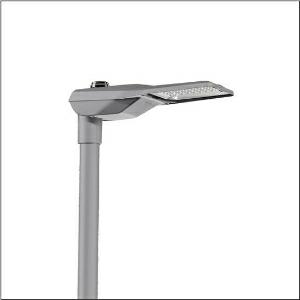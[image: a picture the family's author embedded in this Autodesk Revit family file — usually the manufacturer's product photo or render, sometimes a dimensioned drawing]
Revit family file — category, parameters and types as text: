
# Revit family: streetlight_sl_21_mini___st1_0a_5xe6d37n08hb_abde
name_source: partatom
category: Lighting Fixtures
units: mm (PartAtom-declared; Revit-internal decimal feet)

## family parameters
Cut with Voids When Loaded = No
Host = Face
Light Source = No
Part Type = Normal
Room Calculation Point = No
Round Connector Dimension = Use Diameter
Shared = No

## types (1)
- --- (1 x LED, 9040 lm, 66 W, 3000K)
    Apparent Load = 66 VA
    CIE Flux Codes = 37 72 97 100 100
    Color Rendering = 70
    Color Temperature = 3000K
    Default Elevation = 1800 mm
    Description = Streetlight SL 21 mini, mast luminaire, primary light control with lens, of PMMA, primary optical cover: cover, of toughened safety glass, transparent, light distribution: ST1.0a, light emission: direct distribution, primary light characteristic: asymmetric, installation type: side-entry, LED, 3G 1.5mm², High Power LED, rated luminous flux: 9.040lm, luminous efficacy: 137lm/W, light colour: 730, colour temperature: 3000K, control gear: NEMA (7pin), control: overheat protection, pre-setting: linear dimming characteristic, constant luminous flux control, time-dependent luminous flux control, flexible luminous flux parameterisation, mains connection: 230..240V, AC, 50/60Hz, connection cable pre-assembled, cable length: 8,5m, wiring characteristics: H07RN-F, start of lifetime: 66W, end of service life: 69W, reduction: 30W, luminaire housing, of diecast aluminium (EN AC-44300), powder-coated, Siteco® metallic grey (DB 702S), corrosivity category C5 mid according to DIN EN ISO 12944, multi-level sealing system, sealing non-destructively replaceable, inclination adjustable: 0°, 5°, 10°, 15°, length: 628mm, width: 235mm, height: 110mm, spigot size: 42mm (side-entry), mounting height: 4..8m, protection rating (complete): IP66, insulation class (complete): insulation class I (protective earthing), certification: CE, ENEC, ENEC+, VDE, impact resistance: IK10, permissible operating ambient temperature for outdoor applications: -40..+50°C, standard-compliant lighting for roads and squares, packaging unit: 1 piece

Light Distribution: ST1.0a
    Height = 110 mm
    Lamp = 1 x LED
    Lamp Light Flux = 9040 lm
    Lamp Power = 66 W
    Lamp count = 1
    Length = 625 mm
    Luminous efficacy = 137 lm/W
    Manufacturer = Siteco
    ModVariant = No
    Model = 5XE6D37N08HB
    Number of Poles = 1
    OnlyDefault = Yes
    Power Factor = 1
    Product Name = Streetlight SL 21 mini | ST1.0a
    Product group = mast luminaire | pylon top
    ProductGroupID = 6100
    Protection Class = Protection class I
    Protection Degree = IP 66
    RLX_Detail_Level = 1
    RLX_Emergency_Light_Flux = 0 lm
    RLX_Emergency_Type = 0
    RLX_Emergency_Type_DB = No
    RlxData = <blob elided: 26161 chars, md5=9ac2b51b>
    Socket = socket
    Standby Power = 0 W
    System Light Flux = 9040 lm
    System Power = 66 W
    Type Comments = factory setting: luminous flux: 100 % | dim-lin: 254 | 670 mA
    Type Image = l_1294379.jpg
    URL = http://relux.com
    VarID = @adj_136282
    Voltage = 0 V
    Weight = 0.00 kg
    Width = 234 mm

## geometry (parser evidence)
native form markers: Blend x4, Sweep x11
no freeform markers — native parametric forms only
